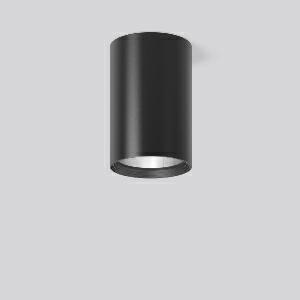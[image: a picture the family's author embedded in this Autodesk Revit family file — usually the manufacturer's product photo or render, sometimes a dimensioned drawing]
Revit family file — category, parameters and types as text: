
# Revit family: heledon_maxi_a_931216_003_3_76_0971
name_source: partatom
category: Lighting Fixtures
units: mm (PartAtom-declared; Revit-internal decimal feet)

## family parameters
Cut with Voids When Loaded = No
Host = Face
Light Source = No
Part Type = Normal
Room Calculation Point = No
Round Connector Dimension = Use Diameter
Shared = No

## types (1)
- HELEDON maxi A (1 x LED Modul 935, 3300 lm, 3500)
    Apparent Load = 25 VA
    Approval mark = CE
    CIE Flux Codes = 100 100 100 100 100
    Color Rendering = 92
    Color Temperature = 3500
    Default Elevation = 1800 mm
    Description = Series: HELEDON maxi
Cylindrical surface-mounted downlight. Housing: die-cast aluminium, powder-coated. Internal ceiling frame polycarbonate with bayonet mounting. Black plastic ring and recessed LED to prevent glare from the side. Optical assembly with reflector made of MIRO-Silver with 98% total light reflection for outstanding efficiency - can be changed without tools. Best colour rendering index Ra>90. Suitable for Ceiling mounting. Easy installation with a separate ceiling frame with bayonet mounting and plug connection. Driver integrated. Connected via plug-in connector. High quality converter without flickering and stroboscopic effect. The following accessories can be mounted without use of tools: interchangeable lenses, decorative glasses, honeycomb louvre, clear and frosted diffusers, white interchangeable plastic ring. 
Colour: deep black, matt (RAL 9005)
Diameter: 123 mm
Height: 183 mm
Lamp: LED
Socket: without socket
Colour temperature: 3500K
Colour rendering index (CRI): 92
System power: 25 W
Rated luminous flux: 3300 lm
Luminous efficiency: 132 lm/W
Control gear: Converter, dimmable, DALI
Protection class: I
Type of protection: IP 20
    Height = 183 mm
    Lamp = 1 x LED Modul 935
    Lamp Light Flux = 3300 lm
    Lamp count = 1
    Length = 123 mm
    Lifetime = 50000 h
    Luminous efficacy = 132 lm/W
    Manufacturer = RZB
    ModVariant = No
    Model = 931216.003.3.76
    Mounting Place = Ceiling
    Mounting Type = Surface mounted
    Number of Poles = 1
    OnlyDefault = Yes
    Power Factor = 1
    Product Name = HELEDON maxi A
    Product group = Surface mounted downlights
    ProductGroupID = 302
    Protection Class = Protection class I
    Protection Degree = IP 20
    RLX_Detail_Level = 1
    RLX_Emergency_Light_Flux = 0 lm
    RLX_Emergency_Type = 0
    RLX_Emergency_Type_DB = No
    RlxData = <blob elided: 100273 chars, md5=d01f3fdb>
    Socket = socket
    Standby Power = 0 W
    System Light Flux = 3300 lm
    System Power = 25 W
    Type Comments = Product without accessories
    Type Image = 931192.003.jpg
    URL = http://relux.com
    VarID = ---
    Voltage = 230 V
    Voltage Range = 220-240 V
    Weight = 0.00 kg
    Width = 0 mm  [stored 0 ft]

note: [stored X ft] marks values corroborated as IEEE doubles in the binary element streams (Revit-internal decimal feet)

## geometry (parser evidence)
native form markers: Blend x4, Sweep x9
no freeform markers — native parametric forms only
